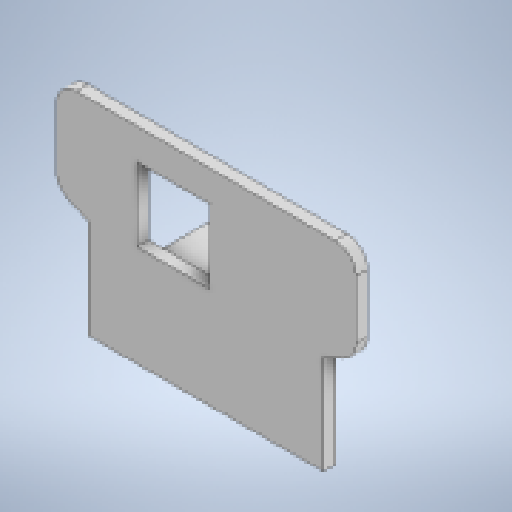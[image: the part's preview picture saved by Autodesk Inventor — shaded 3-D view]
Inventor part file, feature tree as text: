
AUTODESK INVENTOR PART (.ipt)
format: ipt  version: 2023.3 (Build 273359000, 359)  size: 272,896 bytes
history: native  units: mm
features: extrude x3, sketch x3, other x3, reference x1
ambient origin geometry x8: Origin, YZ Plane, XZ Plane, XY Plane, X Axis, Y Axis, Z Axis, Center Point
bodies: Solid1 (feature_tree)
feature tree (10):
  extrude  "Extrusion1"  Depth=0.1mm
  extrude  "Extrusion2"  Depth=0.1mm
  extrude  "Extrusion3"  Depth=0.4mm
  sketch  "Sketch1"  dims[d1=0.1mm d2=0.1mm]
  reference  "Reference1"
  sketch  "Sketch2"  dims[d3=0.1mm d4=0.1mm]
  sketch  "Sketch3"  dims[d5=0.1mm d7=0.1mm d8=0.1mm d9=0.1mm d10=0.1mm d11=0.1mm d13=0.1mm d15=0.1mm d16=0.4mm d17=0.0mm d18=1.05395mm d19=2.75mm d21=2.5mm d22=4.95mm d23=2.5mm d24=0.4mm d25=0.0mm d26=3.0mm d27=0.0mm d28=4.0mm d29=0.4mm]
  parser-record x1  (decoder bookkeeping rows leaked as tree rows — omitted from the tree; the rows remain in map.json)
  other  "np2a_assembly.iam"
  other  "cap_flex_and_headstage:1"
note: 1 file-system path scrubbed to <path> (originals preserved in map.json)
